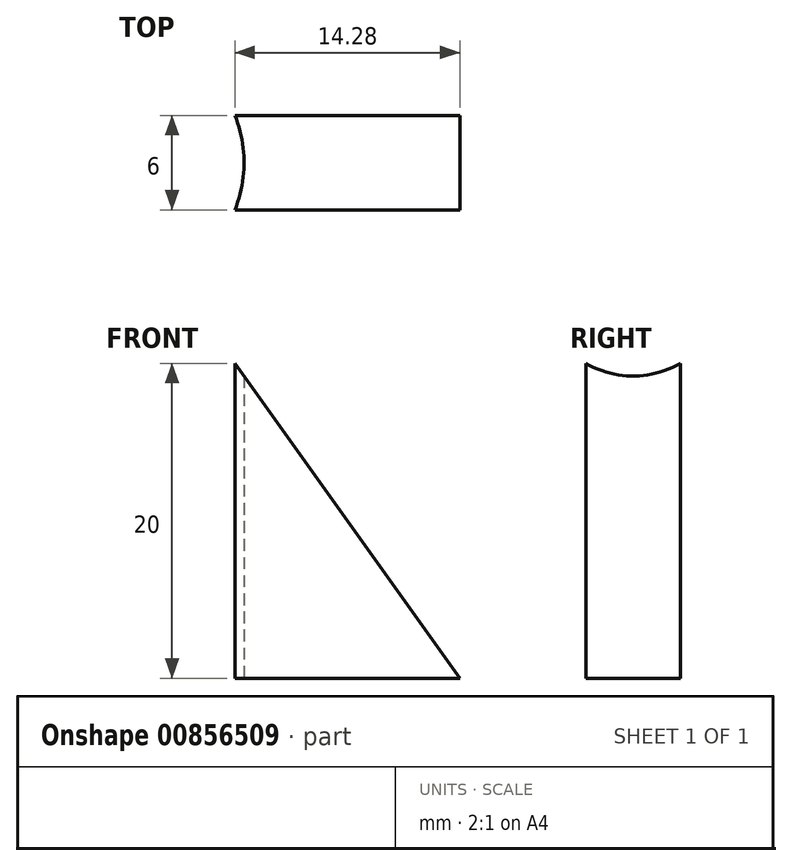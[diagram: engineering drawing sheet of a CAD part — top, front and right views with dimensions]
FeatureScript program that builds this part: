
annotation { "Feature Type Name" : "Feature", "Feature Type Description" : "" }
export const myFeature = defineFeature(function(context is Context, id is Id, definition is map)
    precondition{}
    {
        {
            var Q0;
            Q0=qCreatedBy(makeId("Top.planeOp"),FACE);
            var sketch = newSketch(context, id + "F0", { "sketchPlane" : qUnion([Q0])});
            skLineSegment(sketch, "E0.bottom", {"start": v(7.14, 3) * mm, "end": v(-7.14, 3) * mm});
            skLineSegment(sketch, "E0.top", {"start": v(7.14, -3) * mm, "end": v(-7.14, -3) * mm});
            skLineSegment(sketch, "E0.left", {"start": v(7.14, 3) * mm, "end": v(7.14, -3) * mm});
            skLineSegment(sketch, "E0.right", {"start": v(-7.14, 3) * mm, "end": v(-7.14, -3) * mm});
            skPoint(sketch, "E0.middle", {"position": v(0, 0) * mm});
            skPoint(sketch, "E1", {"position": v(-7.14, 3) * mm});
            skPoint(sketch, "E2", {"position": v(-7.14, -3) * mm});
            skSolve(sketch);
        }
        {
            var Q0;
            Q0=makeQuery(id+"F0.imprint","IMPRINT",FACE,{"disambiguationData":[TD([[makeQuery(id+"F0.imprint","IMPRINT",EDGE,{"derivedFrom":sQuery(id+"F0.wireOp",EDGE,"E0.bottom")}),1.0]])]});
            extrude(context, id + "F1", {"entities" : qUnion([Q0]), "depth" : 20 * mm, "offsetDistance" : 25 * mm});
        }
        {
            var Q0;
            Q0=makeQuery(id+"F1.opExtrude","CAP_EDGE",EDGE,{"disambiguationData":[OSD([sQuery(id+"F0.wireOp",EDGE,"E0.left")])],"isStart":false});
            chamfer(context, id + "F2", {"entities" : qUnion([Q0]), "chamferType" : ChamferType.TWO_OFFSETS, "width1" : 20 * mm, "oppositeDirection" : false, "width2" : 14.28 * mm, "tangentPropagation" : true});
        }
        {
            var Q0;
            Q0=qCreatedBy(makeId("Top.planeOp"),FACE);
            var sketch = newSketch(context, id + "F3", { "sketchPlane" : qUnion([Q0])});
            skLineSegment(sketch, "E3.bottom", {"start": v(-7.14, -3) * mm, "end": v(7.14, -3) * mm});
            skLineSegment(sketch, "E3.top", {"start": v(-7.14, 3) * mm, "end": v(7.14, 3) * mm});
            skLineSegment(sketch, "E3.left", {"start": v(-7.14, -3) * mm, "end": v(-7.14, 3) * mm});
            skLineSegment(sketch, "E3.right", {"start": v(7.14, -3) * mm, "end": v(7.14, 3) * mm});
            skPoint(sketch, "E3.middle", {"position": v(0, 0) * mm});
            skCircle(sketch, "E4", {"center": v(-14.56, 0) * mm, "radius": 8 * mm});
            skSolve(sketch);
        }
        {
            var Q0;
            {var subQ0=sQuery(id+"F3.wireOp",EDGE,"E3.left");Q0=makeQuery(id+"F3.imprint","IMPRINT",FACE,{"disambiguationData":[TD([[makeQuery(id+"F3.imprint","IMPRINT",EDGE,{"derivedFrom":subQ0}),1.0]])]});}
            var Q1;
            {var subQ0=sQuery(id+"F3.wireOp",EDGE,"E3.left");Q1=makeQuery(id+"F3.imprint","IMPRINT",FACE,{"disambiguationData":[TD([[makeQuery(id+"F3.imprint","IMPRINT",EDGE,{"derivedFrom":subQ0}),-1.0]])]});}
            extrude(context, id + "F4", {"entities" : qUnion([Q0, Q1]), "operationType" : NewBodyOperationType.REMOVE, "depth" : 25 * mm, "offsetDistance" : 25 * mm});
        }
    });
